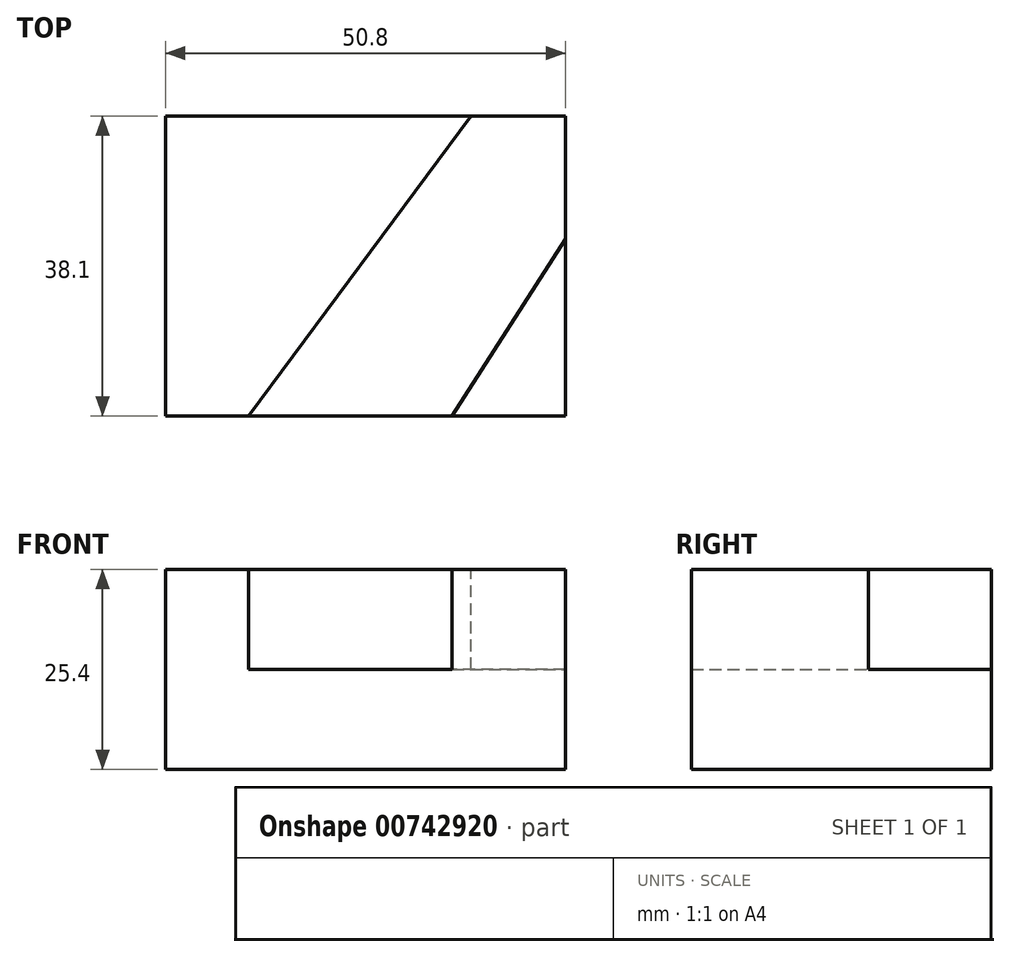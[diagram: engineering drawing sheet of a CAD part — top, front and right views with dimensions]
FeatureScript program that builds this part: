
annotation { "Feature Type Name" : "Feature", "Feature Type Description" : "" }
export const myFeature = defineFeature(function(context is Context, id is Id, definition is map)
    precondition{}
    {
        {
            var Q0;
            Q0=qCreatedBy(makeId("Front.planeOp"),FACE);
            var sketch = newSketch(context, id + "F0", { "sketchPlane" : qUnion([Q0])});
            skLineSegment(sketch, "E0.bottom", {"start": v(0, 0) * mm, "end": v(50.8, 0) * mm});
            skLineSegment(sketch, "E0.top", {"start": v(0, 25.4) * mm, "end": v(50.8, 25.4) * mm});
            skLineSegment(sketch, "E0.left", {"start": v(0, 0) * mm, "end": v(0, 25.4) * mm});
            skLineSegment(sketch, "E0.right", {"start": v(50.8, 0) * mm, "end": v(50.8, 25.4) * mm});
            skSolve(sketch);
        }
        {
            var Q0;
            Q0=makeQuery(id+"F0.imprint","IMPRINT",FACE,{"disambiguationData":[TD([[makeQuery(id+"F0.imprint","IMPRINT",EDGE,{"derivedFrom":sQuery(id+"F0.wireOp",EDGE,"E0.bottom")}),1.0]])]});
            extrude(context, id + "F1", {"entities" : qUnion([Q0]), "depth" : 38.1 * mm, "offsetDistance" : 25.4 * mm});
        }
        {
            var Q0;
            Q0=makeQuery(id+"F1.opExtrude","SWEPT_FACE",FACE,{"disambiguationData":[OSD([sQuery(id+"F0.wireOp",EDGE,"E0.top")])]});
            var sketch = newSketch(context, id + "F2", { "sketchPlane" : qUnion([Q0])});
            skLineSegment(sketch, "E1", {"start": v(10.51, -38.1) * mm, "end": v(38.8, 0) * mm});
            skLineSegment(sketch, "E2", {"start": v(38.8, 0) * mm, "end": v(50.8, 0) * mm});
            skLineSegment(sketch, "E3", {"start": v(50.8, 0) * mm, "end": v(50.8, -15.6) * mm});
            skLineSegment(sketch, "E4", {"start": v(50.8, -15.6) * mm, "end": v(36.38, -38.1) * mm});
            skLineSegment(sketch, "E5", {"start": v(36.38, -38.1) * mm, "end": v(10.51, -38.1) * mm});
            skSolve(sketch);
        }
        {
            var Q0;
            Q0=makeQuery(id+"F2.imprint","IMPRINT",FACE,{"disambiguationData":[TD([[makeQuery(id+"F2.imprint","IMPRINT",EDGE,{"derivedFrom":sQuery(id+"F2.wireOp",EDGE,"E1")}),-1.0]])]});
            extrude(context, id + "F3", {"entities" : qUnion([Q0]), "operationType" : NewBodyOperationType.REMOVE, "oppositeDirection" : true, "depth" : 12.7 * mm, "offsetDistance" : 25.4 * mm});
        }
    });
